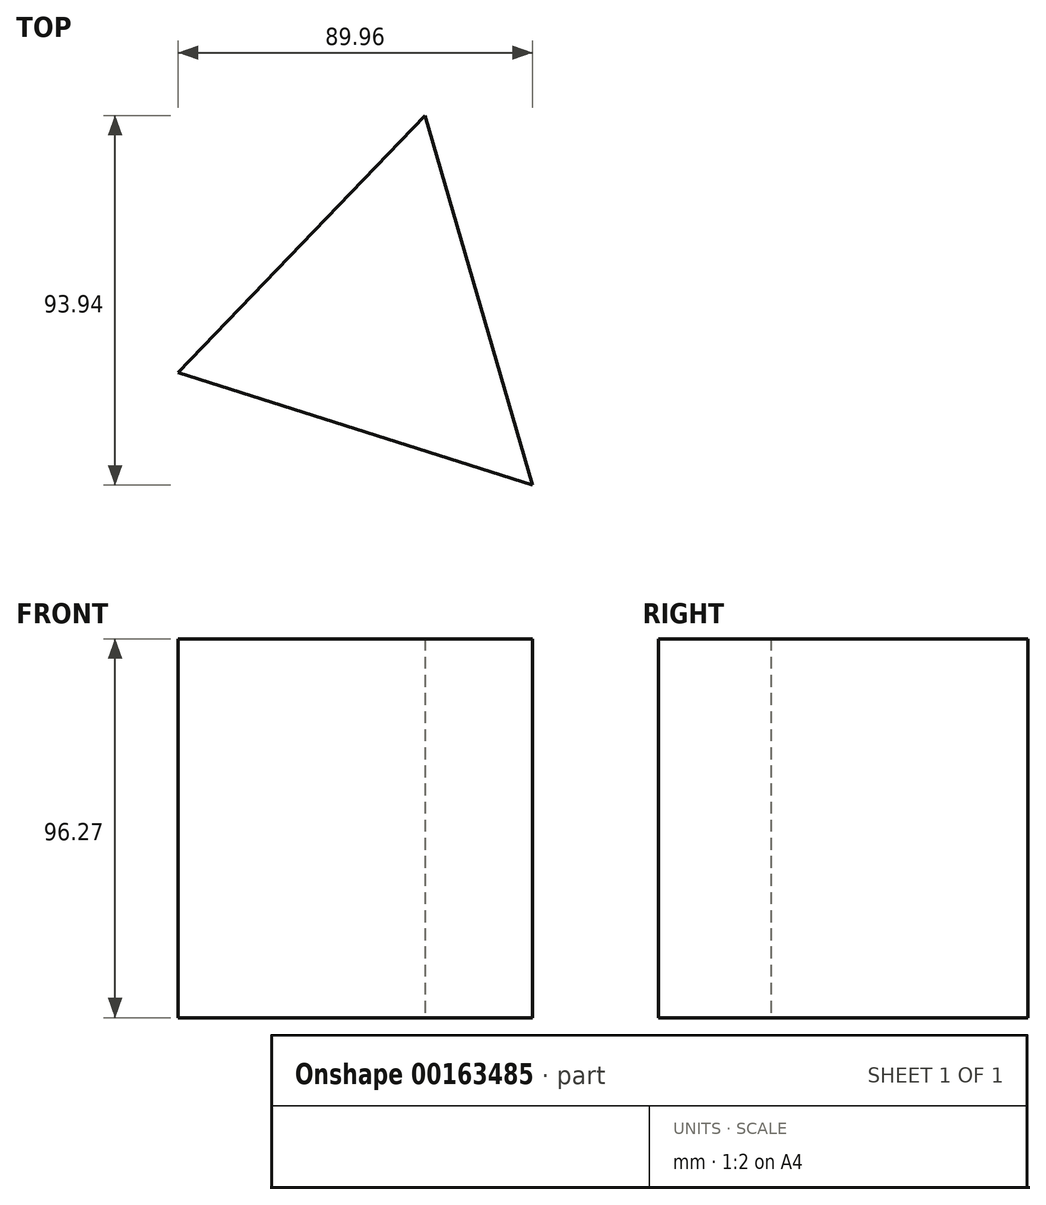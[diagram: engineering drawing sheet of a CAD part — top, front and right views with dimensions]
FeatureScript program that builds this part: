
annotation { "Feature Type Name" : "Feature", "Feature Type Description" : "" }
export const myFeature = defineFeature(function(context is Context, id is Id, definition is map)
    precondition{}
    {
        {
            var Q0;
            Q0=qCreatedBy(makeId("Top.planeOp"),FACE);
            var sketch = newSketch(context, id + "F0", { "sketchPlane" : qUnion([Q0])});
            skLineSegment(sketch, "E0", {"start": v(40.37, 75.81) * mm, "end": v(130.33, 47.13) * mm});
            skLineSegment(sketch, "E1", {"start": v(130.33, 47.13) * mm, "end": v(103.09, 141.07) * mm});
            skLineSegment(sketch, "E2", {"start": v(103.09, 141.07) * mm, "end": v(40.37, 75.81) * mm});
            skSolve(sketch);
        }
        {
            var Q0;
            Q0 = qSketchRegion(id + "F0", true);
            extrude(context, id + "F1", {"entities" : qUnion([Q0]), "depth" : 96.27 * mm});
        }
    });
